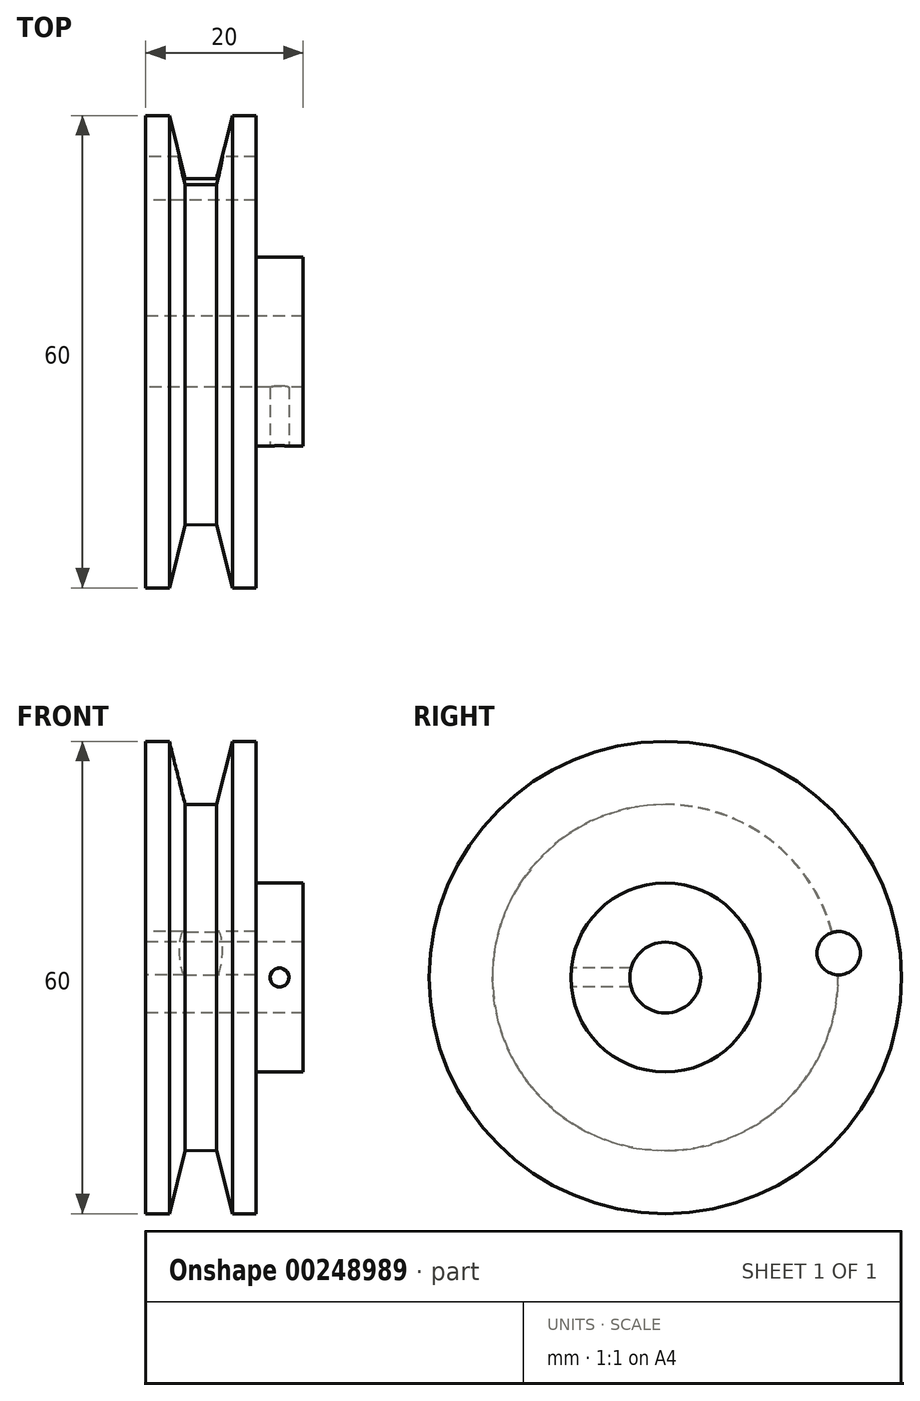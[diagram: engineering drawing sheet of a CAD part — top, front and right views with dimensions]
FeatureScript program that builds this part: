
annotation { "Feature Type Name" : "Feature", "Feature Type Description" : "" }
export const myFeature = defineFeature(function(context is Context, id is Id, definition is map)
    precondition{}
    {
        {
            var Q0;
            Q0=qCreatedBy(makeId("Front.planeOp"),FACE);
            var sketch = newSketch(context, id + "F0", { "sketchPlane" : qUnion([Q0])});
            skLineSegment(sketch, "E0", {"start": v(-21.59, 0) * mm, "end": v(21.59, 0) * mm});
            skLineSegment(sketch, "E1", {"start": v(-7, 4.5) * mm, "end": v(-7, 30) * mm});
            skLineSegment(sketch, "E2", {"start": v(-7, 30) * mm, "end": v(-4, 30) * mm});
            skLineSegment(sketch, "E3", {"start": v(2, 21.95) * mm, "end": v(4, 30) * mm});
            skLineSegment(sketch, "E4", {"start": v(4, 30) * mm, "end": v(7, 30) * mm});
            skLineSegment(sketch, "E5", {"start": v(7, 30) * mm, "end": v(7, 12) * mm});
            skPoint(sketch, "E6.end.orphan", {"position": v(0, 13.96) * mm});
            skLineSegment(sketch, "E7", {"start": v(-4, 30) * mm, "end": v(-2, 22) * mm});
            skLineSegment(sketch, "E8.trimOffspring", {"start": v(-2, 22) * mm, "end": v(2, 21.95) * mm});
            skLineSegment(sketch, "E9", {"start": v(7, 12) * mm, "end": v(13, 12) * mm});
            skLineSegment(sketch, "E10", {"start": v(13, 12) * mm, "end": v(13, 4.5) * mm});
            skLineSegment(sketch, "E11", {"start": v(-7, 4.5) * mm, "end": v(13, 4.5) * mm});
            skSolve(sketch);
        }
        {
            var Q0;
            Q0=makeQuery(id+"F0.imprint","IMPRINT",FACE,{"disambiguationData":[TD([[makeQuery(id+"F0.imprint","IMPRINT",EDGE,{"derivedFrom":sQuery(id+"F0.wireOp",EDGE,"E1")}),-1.0]])]});
            var Q1;
            Q1=sQuery(id+"F0.wireOp",EDGE,"E0");
            revolve(context, id + "F1", {"entities" : qUnion([Q0]), "axis" : qUnion([Q1]), "revolveType" : RevolveType.FULL});
        }
        {
            var Q0;
            Q0=makeQuery(id+"F1.opRevolve","SWEPT_FACE",FACE,{"disambiguationData":[OSD([sQuery(id+"F0.wireOp",EDGE,"E1")])]});
            var sketch = newSketch(context, id + "F2", { "sketchPlane" : qUnion([Q0])});
            skPoint(sketch, "E12", {"position": v(-22.02, 3.09) * mm});
            skSolve(sketch);
        }
        {
            var Q0;
            Q0=sQuery(id+"F2.wireOp",VERTEX,"E12");
            var Q1;
            Q1=makeQuery(id+"F1.opRevolve","SWEPT_BODY",BODY,{"disambiguationData":[OSD([sQuery(id+"F0.wireOp",EDGE,"E1"),sQuery(id+"F0.wireOp",EDGE,"E2"),sQuery(id+"F0.wireOp",EDGE,"E3"),sQuery(id+"F0.wireOp",EDGE,"E4"),sQuery(id+"F0.wireOp",EDGE,"E5"),sQuery(id+"F0.wireOp",EDGE,"E7"),sQuery(id+"F0.wireOp",EDGE,"E8.trimOffspring"),sQuery(id+"F0.wireOp",EDGE,"E9"),sQuery(id+"F0.wireOp",EDGE,"E10"),sQuery(id+"F0.wireOp",EDGE,"E11")])]});
            hole(context, id + "F3", {"style" : HoleStyle.SIMPLE, "endStyle" : HoleEndStyle.BLIND, "standardTappedOrClearance" : lookupTablePath({ "standard" : "ISO", "fit" : "Normal", "size" : "M5", "type" : "Clearance" }), "standardBlindInLast" : lookupTablePath({ "fit" : "Standard", "standard" : "ISO", "size" : "M5", "type" : "Clearance" }), "holeDiameter" : 5.5 * mm, "holeDepth" : 14 * mm, "tappedDepth" : 11.6 * mm, "tapClearance" : 3, "startFromSketch" : true, "locations" : qUnion([Q0]), "scope" : qUnion([Q1])});
        }
        {
            var Q0;
            Q0=qCreatedBy(makeId("Front.planeOp"),FACE);
            cPlane(context, id + "F4", {"entities" : qUnion([Q0]), "cplaneType" : CPlaneType.OFFSET, "offset" : 12 * mm, "width" : 150 * mm, "height" : 150 * mm});
        }
        {
            var Q0;
            Q0=qCreatedBy(id+"F4.planeOp",FACE);
            var sketch = newSketch(context, id + "F5", { "sketchPlane" : qUnion([Q0])});
            skPoint(sketch, "E13", {"position": v(10, 0) * mm});
            skLineSegment(sketch, "E14", {"start": v(4, 30) * mm, "end": v(7, 30) * mm});
            skLineSegment(sketch, "E15", {"start": v(7, -30) * mm, "end": v(4, -30) * mm});
            skSolve(sketch);
        }
        {
            var Q0;
            Q0=sQuery(id+"F5.wireOp",VERTEX,"E13");
            var Q1;
            Q1=makeQuery(id+"F1.opRevolve","SWEPT_BODY",BODY,{"disambiguationData":[OSD([sQuery(id+"F0.wireOp",EDGE,"E1"),sQuery(id+"F0.wireOp",EDGE,"E2"),sQuery(id+"F0.wireOp",EDGE,"E3"),sQuery(id+"F0.wireOp",EDGE,"E4"),sQuery(id+"F0.wireOp",EDGE,"E5"),sQuery(id+"F0.wireOp",EDGE,"E7"),sQuery(id+"F0.wireOp",EDGE,"E8.trimOffspring"),sQuery(id+"F0.wireOp",EDGE,"E9"),sQuery(id+"F0.wireOp",EDGE,"E10"),sQuery(id+"F0.wireOp",EDGE,"E11")])]});
            hole(context, id + "F6", {"style" : HoleStyle.SIMPLE, "endStyle" : HoleEndStyle.BLIND, "standardTappedOrClearance" : lookupTablePath({ "standard" : "ISO", "engagement" : "75%", "pitch" : "0.6 mm", "size" : "M3", "type" : "Tapped" }), "standardBlindInLast" : lookupTablePath({ "standard" : "ISO", "engagement" : "75%", "pitch" : "0.6 mm", "size" : "M3", "type" : "Tapped" }), "holeDiameter" : 2.4 * mm, "showTappedDepth" : true, "holeDepth" : 13.4 * mm, "tappedDepth" : 11.6 * mm, "tapClearance" : 3, "startFromSketch" : true, "locations" : qUnion([Q0]), "scope" : qUnion([Q1])});
        }
    });
